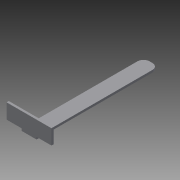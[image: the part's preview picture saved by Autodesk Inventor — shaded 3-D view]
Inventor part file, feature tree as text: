
AUTODESK INVENTOR PART (.ipt)
format: ipt  version: 2015 (Build 190159000, 159)  size: 92,160 bytes
history: native  units: mm
features: extrude x3, sketch x3, other x1, fillet x1
ambient origin geometry x8: Origin, YZ Plane, XZ Plane, XY Plane, X Axis, Y Axis, Z Axis, Center Point
bodies: Body1 (feature_tree)
feature tree (8):
  other  "ソリッド1"
  extrude  "押し出し1"  Depth=10.0mm
  fillet  "フィレット1"  Radius=80.0mm
  extrude  "押し出し2"  Depth=1.5mm TaperAngle=0.0deg
  extrude  "押し出し4"  Depth=4.0mm
  sketch  "スケッチ1"
  sketch  "スケッチ2"
  sketch  "スケッチ4"
